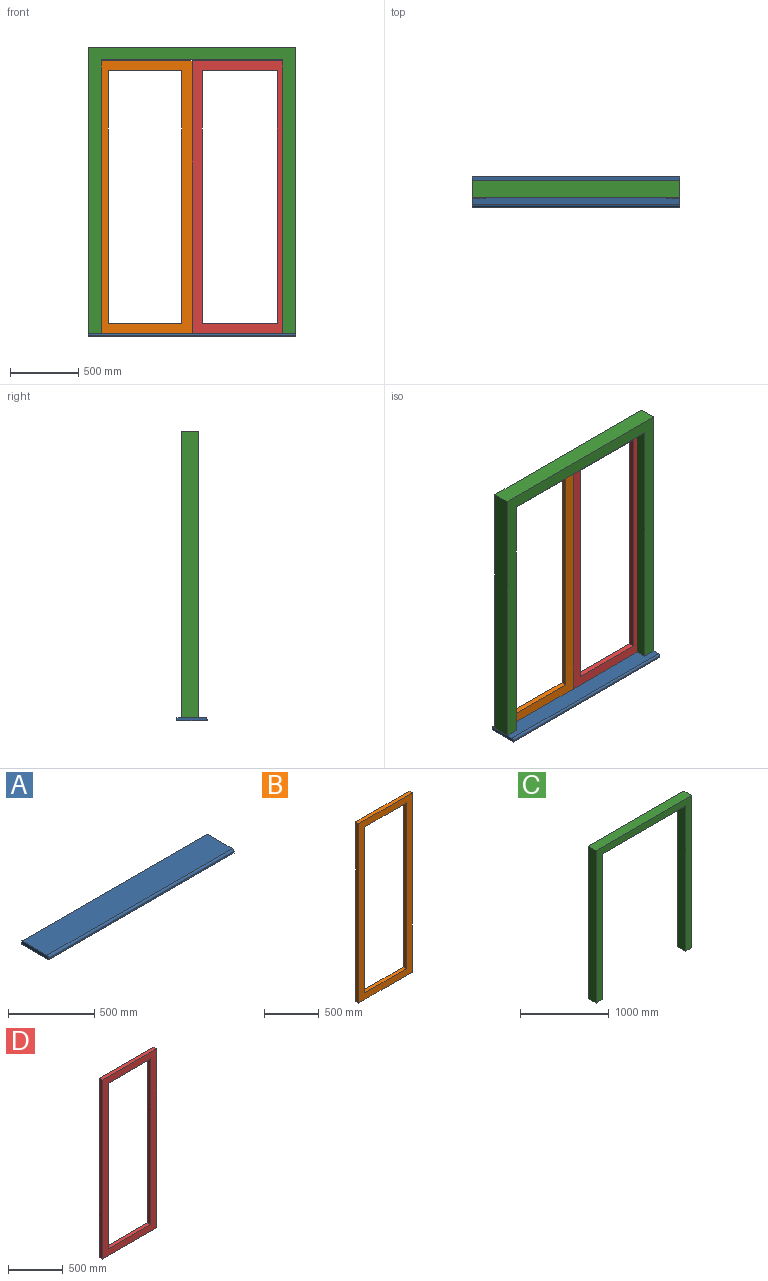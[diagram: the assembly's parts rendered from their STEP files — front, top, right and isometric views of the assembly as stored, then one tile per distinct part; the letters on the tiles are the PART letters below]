
ASSEMBLY  parts=4 mates=6
PART A: 7 faces, bbox 1520x220x25 mm
  f0: plane 1520x10mm, normal (0,-1,0), area 15200mm2, adj f1,f3,f5,f6
  f1: plane 220x25mm, normal (1,0,0), area 5451.7mm2, adj f0,f2,f4,f5,f6
  f2: plane 1520x25mm, normal (0,1,0), area 38000mm2, adj f1,f3,f4,f5
  f3: plane 220x25mm, normal (-1,0,0), area 5451.7mm2, adj f0,f2,f4,f5,f6
  f4: plane 1520x205mm, normal (0,0,1), area 311600mm2, adj f1,f2,f3,f6
  f5: plane 1520x220mm, normal (0,0,-1), area 334400mm2, adj f0,f1,f2,f3
  f6: cylinder r=15mm len=1520mm, axis (-1,0,0), area 35814.2mm2, adj f0,f1,f3,f4
PART B: 10 faces, bbox 690x40x2000 mm
  f0: plane 2000x40mm, normal (1,0,0), area 80000mm2, adj f1,f3,f4,f5
  f1: plane 690x40mm, normal (0,0,1), area 27600mm2, adj f0,f2,f4,f5
  f2: plane 2000x40mm, normal (-1,0,0), area 80000mm2, adj f1,f3,f4,f5
  f3: plane 690x40mm, normal (0,0,-1), area 27600mm2, adj f0,f2,f4,f5
  f4: plane 2000x690mm, normal (0,-1,0), area 381000mm2, adj f0,f1,f2,f3,f6,f7,f8,f9
  f5: plane 2000x690mm, normal (0,1,0), area 381000mm2, adj f0,f1,f2,f3,f6,f7,f8,f9
  f6: plane 1850x40mm, normal (1,0,0), area 74000mm2, adj f4,f5,f7,f9
  f7: plane 540x40mm, normal (0,0,1), area 21600mm2, adj f4,f5,f6,f8
  f8: plane 1850x40mm, normal (-1,0,0), area 74000mm2, adj f4,f5,f7,f9
  f9: plane 540x40mm, normal (0,0,-1), area 21600mm2, adj f4,f5,f6,f8
PART C: 10 faces, bbox 1520x125x2100 mm
  f0: plane 1330x125mm, normal (0,0,-1), area 166250mm2, adj f1,f7,f8,f9
  f1: plane 2005x125mm, normal (-1,0,0), area 250625mm2, adj f0,f2,f8,f9
  f2: plane 125x95mm, normal (0,0,-1), area 11875mm2, adj f1,f3,f8,f9
  f3: plane 2100x125mm, normal (1,0,0), area 262500mm2, adj f2,f4,f8,f9
  f4: plane 1520x125mm, normal (0,0,1), area 190000mm2, adj f3,f5,f8,f9
  f5: plane 2100x125mm, normal (-1,0,0), area 262500mm2, adj f4,f6,f8,f9
  f6: plane 125x95mm, normal (0,0,-1), area 11875mm2, adj f5,f7,f8,f9
  f7: plane 2005x125mm, normal (1,0,0), area 250625mm2, adj f0,f6,f8,f9
  f8: plane 2100x1520mm, normal (0,-1,0), area 525350mm2, adj f0,f1,f2,f3,f4,f5,f6,f7
  f9: plane 2100x1520mm, normal (0,1,0), area 525350mm2, adj f0,f1,f2,f3,f4,f5,f6,f7
PART D: 10 faces, bbox 700x40x2000 mm
  f0: plane 2000x40mm, normal (1,0,0), area 80000mm2, adj f1,f3,f4,f5
  f1: plane 700x40mm, normal (0,0,1), area 28000mm2, adj f0,f2,f4,f5
  f2: plane 2000x40mm, normal (-1,0,0), area 80000mm2, adj f1,f3,f4,f5
  f3: plane 700x40mm, normal (0,0,-1), area 28000mm2, adj f0,f2,f4,f5
  f4: plane 2000x700mm, normal (0,-1,0), area 382500mm2, adj f0,f1,f2,f3,f6,f7,f8,f9
  f5: plane 2000x700mm, normal (0,1,0), area 382500mm2, adj f0,f1,f2,f3,f6,f7,f8,f9
  f6: plane 1850x40mm, normal (1,0,0), area 74000mm2, adj f4,f5,f7,f9
  f7: plane 550x40mm, normal (0,0,1), area 22000mm2, adj f4,f5,f6,f8
  f8: plane 1850x40mm, normal (-1,0,0), area 74000mm2, adj f4,f5,f7,f9
  f9: plane 550x40mm, normal (0,0,-1), area 22000mm2, adj f4,f5,f6,f8
PLACE A at identity fixed
PLACE B t=(-1105,-40,1025)mm
PLACE C t=(-760,-30,1075)mm
PLACE D t=(-410,-40,1025)mm
MATE fastened A.f4 <-> B.f3  axis (0,0,1) through (-760,0,25)mm
MATE fastened A.f4 <-> D.f3  axis (0,0,1) through (-760,0,25)mm
MATE planar D.f4 <-> B.f4  axis (0,-1,0) through (-760,-80,2025)mm
MATE fastened A.f4 <-> C.f2  axis (0,0,1) through (0,0,25)mm
MATE planar B.f4 <-> D.f4  axis (0,-1,0) through (-760,-80,25)mm
MATE planar D.f1 <-> B.f1  axis (0,0,1) through (-760,-40,2025)mm
